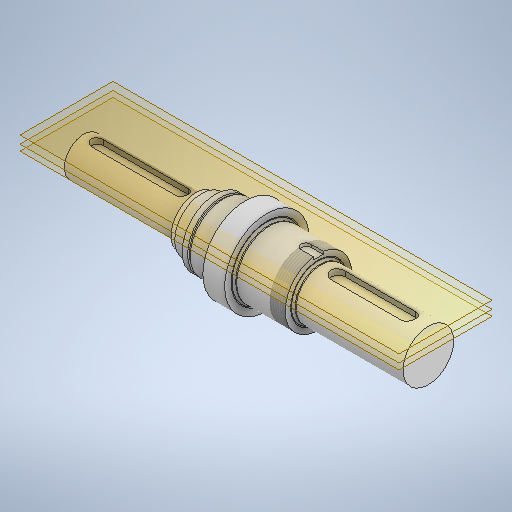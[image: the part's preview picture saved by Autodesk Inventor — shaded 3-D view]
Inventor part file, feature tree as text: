
AUTODESK INVENTOR PART (.ipt)
format: ipt  version: 2025.3 (Build 293356030, 356C)  size: 431,616 bytes
history: native  units: mm
features: sketch x11, revolve x8, plane x3, extrude x3, chamfer x1, thread x1
ambient origin geometry x8: Origin, YZ Plane, XZ Plane, XY Plane, X Axis, Y Axis, Z Axis, Center Point
bodies: Body1 (feature_tree)
feature tree (27):
  revolve  "Umdrehung35"
  plane  "Arbeitsebene8"
  extrude  "Extrusion8"  Depth=16.0mm
  revolve  "Umdrehung36"
  revolve  "Umdrehung37"
  chamfer  "Fasen3"  Distance=5.0mm
  revolve  "Umdrehung38"
  revolve  "Umdrehung39"
  revolve  "Umdrehung40"
  revolve  "Umdrehung41"
  thread  "Gewinde2"  [1 undecoded]
  plane  "Arbeitsebene9"
  extrude  "Extrusion9"  Depth=1.75mm
  plane  "Arbeitsebene10"
  extrude  "Extrusion10"  TaperAngle=0.0deg  [1 undecoded]
  revolve  "Umdrehung42"
  sketch  "Skizze42"  dims[d63=0.0mm d64=16.0mm d65=5.0mm d66=0.0mm d67=0.0mm]
  sketch  "Skizze43"  dims[d68=0.0mm d69=1.75mm d70=0.125mm d71=19.198622mm]
  sketch  "Skizze44"  dims[d72=0.0mm d73=0.0mm]
  sketch  "Skizze45"  dims[d74=0.0mm]
  sketch  "Skizze46"  dims[d75=0.0mm]
  sketch  "Skizze47"  dims[d76=13.0mm d77=0.0mm]
  sketch  "Skizze48"  dims[d78=27.5mm]
  sketch  "Skizze49"  dims[d79=2.5mm d80=0.0mm]
  sketch  "Skizze50"  dims[d81=21.0mm]
  sketch  "Skizze51"  dims[d82=5.0mm d83=0.0mm]
  sketch  "Skizze52"  dims[d84=0.0mm]
note: 2 required parameter values undecoded (feature->parameter linkage not recoverable at this tier; creation-order binding heuristic only, values carry confidence <= 0.55)
